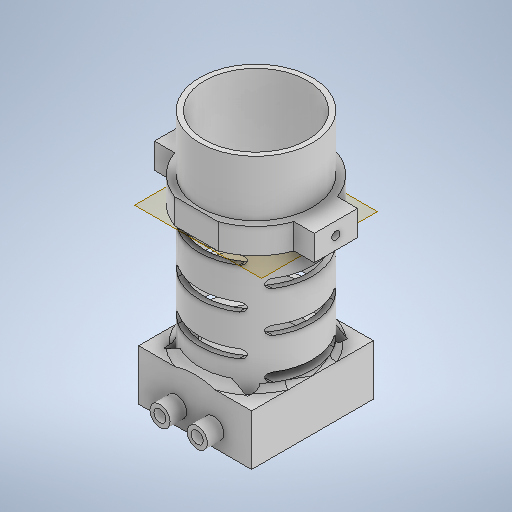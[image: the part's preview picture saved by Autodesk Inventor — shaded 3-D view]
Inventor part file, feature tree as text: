
AUTODESK INVENTOR PART (.ipt)
format: ipt  version: 2025 (Build 290162010, 162A)  size: 671,232 bytes
history: native  units: in
note: dims shown in document units (in); Inventor stores cm internally (conversion verified against a paired STEP export)
features: extrude x11, sketch x11, plane x4, fillet x2, other x1, chamfer x1
ambient origin geometry x8: Origin, YZ Plane, XZ Plane, XY Plane, X Axis, Y Axis, Z Axis, Center Point
bodies: Volumenkörper1 (feature_tree)
feature tree (30):
  extrude  "Extrusion1"  Depth=1.2598in
  extrude  "Extrusion2"  Depth=1.5551in
  extrude  "Extrusion4"  Depth=0.7874in TaperAngle=0.0deg
  other  "Verdickung1"
  fillet  "Rundung4"  Radius=0.0787in
  chamfer  "Fasen4"  Distance=3.0512in
  extrude  "Extrusion9"  Depth=0.0787in
  extrude  "Extrusion10"  Depth=0.0787in
  extrude  "Extrusion11"  Depth=0.2559in TaperAngle=0.0deg
  plane  "Arbeitsebene1"
  extrude  "Extrusion12"  Depth=0.5787in
  plane  "Arbeitsebene2"
  extrude  "Extrusion13"  Depth=0.2559in TaperAngle=0.0deg
  plane  "Arbeitsebene3"
  extrude  "Extrusion14"  TaperAngle=0.0deg  [1 undecoded]
  fillet  "Rundung5"  Radius=0.1378in
  extrude  "Extrusion16"  TaperAngle=0.0deg  [1 undecoded]
  plane  "Arbeitsebene4"
  extrude  "Extrusion17"  Depth=0.3937in
  sketch  "Skizze1"  dims[d0=1.752in d1=1.2598in]
  sketch  "Skizze2"  dims[d2=0.0787in d3=0.0in d4=1.5551in]
  sketch  "Skizze4"  dims[d5=1.2992in d7=0.7874in d8=0.0in d15=0.0787in d16=3.0512in d17=0.0in]
  sketch  "Skizze10"  dims[d40=0.0787in d41=0.0787in]
  sketch  "Skizze11"  dims[d47=1.8898in d53=0.0787in]
  sketch  "Skizze12"  dims[d54=0.1181in d55=0.0787in d56=45.0deg d57=0.2559in d58=0.0in]
  sketch  "Skizze13"  dims[d59=0.5217in d60=0.5787in]
  sketch  "Skizze14"  dims[d61=0.315in d62=0.2559in d63=0.0in]
  sketch  "Skizze15"  dims[d64=0.187in d65=0.0in d66=0.0in d67=0.1378in]
  sketch  "Skizze17"  dims[d68=0.0787in d71=0.0in d72=0.0in]
  sketch  "Skizze18"  dims[d73=0.4921in d74=0.4921in d75=1.1024in d76=0.1378in d77=0.3937in d78=1.1024in d80=0.4921in d81=0.0in d82=0.0in d83=0.4921in d84=-1.2598in d85=0.9843in d86=0.3937in d87=0.0in d89=0.0591in d90=0.0in d91=0.0787in d92=0.9252in d93=0.315in d99=0.128in d102=0.3937in d103=0.0in d104=1.7323in d105=0.0787in d106=0.0in d107=0.0197in d108=0.0344in d109=0.0197in d110=0.0344in]
note: 2 required parameter values undecoded (feature->parameter linkage not recoverable at this tier; creation-order binding heuristic only, values carry confidence <= 0.55)
